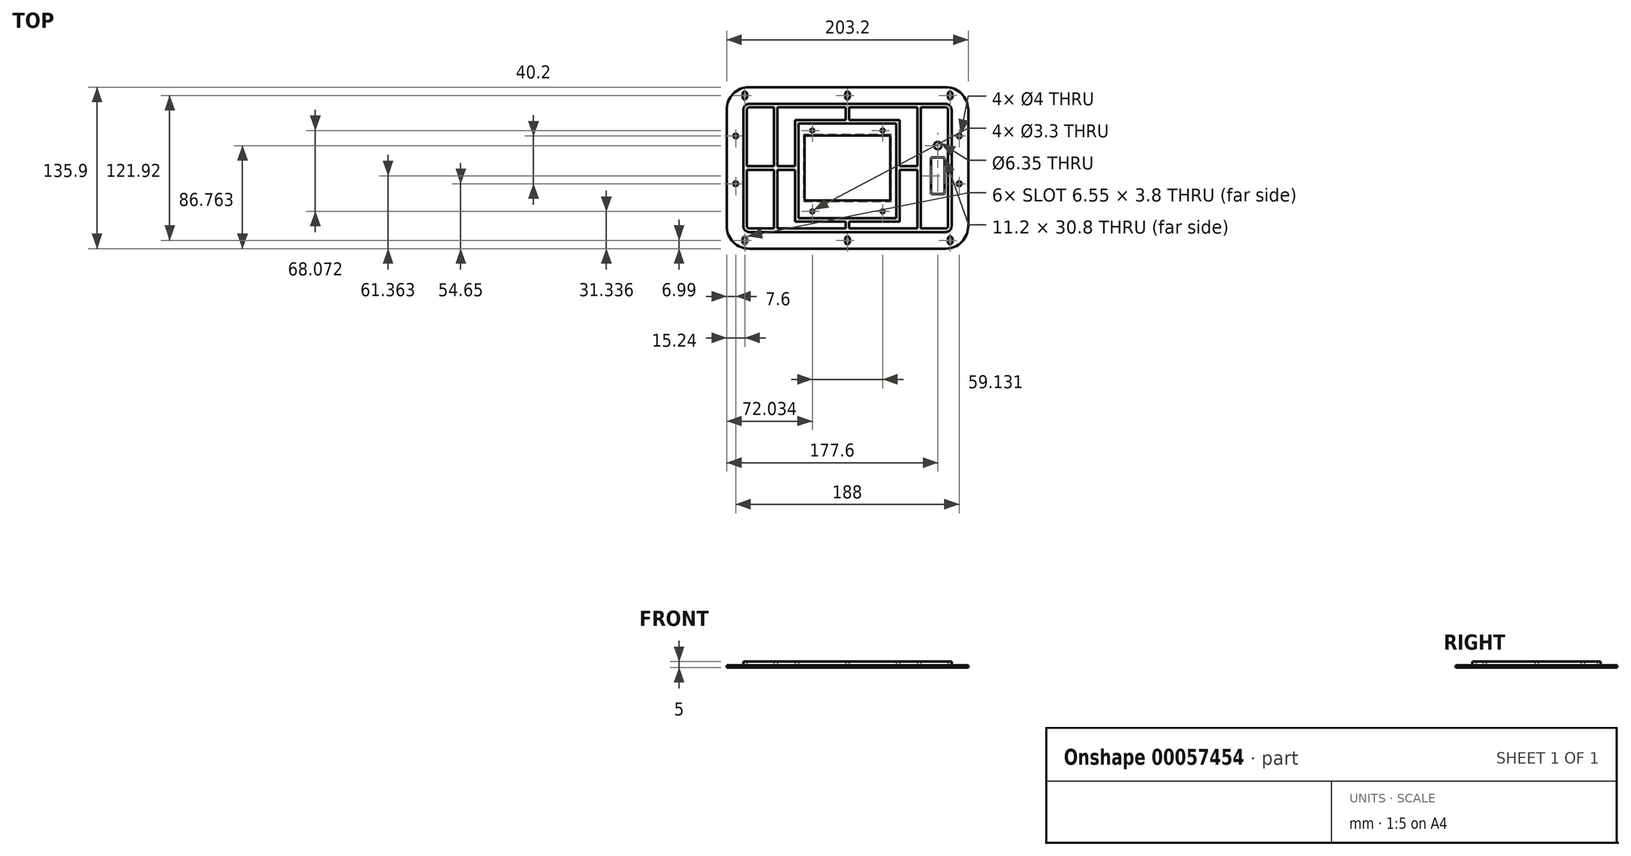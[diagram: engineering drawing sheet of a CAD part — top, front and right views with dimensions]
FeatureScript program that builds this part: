
annotation { "Feature Type Name" : "Feature", "Feature Type Description" : "" }
export const myFeature = defineFeature(function(context is Context, id is Id, definition is map)
    precondition{}
    {
        {
            var Q0;
            Q0=qCreatedBy(makeId("Top.planeOp"),FACE);
            var sketch = newSketch(context, id + "F0", { "sketchPlane" : qUnion([Q0])});
            skLineSegment(sketch, "E0.rect.bottom", {"start": v(82.55, -67.95) * mm, "end": v(-82.55, -67.95) * mm});
            skLineSegment(sketch, "E0.rect.top", {"start": v(82.55, 67.95) * mm, "end": v(-82.55, 67.95) * mm});
            skLineSegment(sketch, "E0.rect.left", {"start": v(101.6, -48.9) * mm, "end": v(101.6, 48.9) * mm});
            skLineSegment(sketch, "E0.rect.right", {"start": v(-101.6, -48.9) * mm, "end": v(-101.6, 48.9) * mm});
            skPoint(sketch, "E0.rect.middle", {"position": v(0, 0) * mm});
            skPoint(sketch, "E1.visualSharp", {"position": v(101.6, -67.94) * mm});
            skArc(sketch, "E1.filletArc", {"start": v(82.55, -67.95) * mm, "mid": v(96.02, -62.37) * mm, "end": v(101.6, -48.9) * mm});
            skPoint(sketch, "E2.visualSharp", {"position": v(101.6, 67.95) * mm});
            skArc(sketch, "E2.filletArc", {"start": v(101.6, 48.9) * mm, "mid": v(96.02, 62.37) * mm, "end": v(82.55, 67.95) * mm});
            skPoint(sketch, "E3.visualSharp", {"position": v(-101.6, 67.95) * mm});
            skArc(sketch, "E3.filletArc", {"start": v(-82.55, 67.95) * mm, "mid": v(-96.02, 62.37) * mm, "end": v(-101.6, 48.9) * mm});
            skPoint(sketch, "E4.visualSharp", {"position": v(-101.6, -67.95) * mm});
            skArc(sketch, "E4.filletArc", {"start": v(-101.6, -48.9) * mm, "mid": v(-96.02, -62.37) * mm, "end": v(-82.55, -67.95) * mm});
            skLineSegment(sketch, "E5", {"start": v(0, 60.96) * mm, "end": v(0, -60.96) * mm, "construction": true});
            skLineSegment(sketch, "E6", {"start": v(-86.36, -59.59) * mm, "end": v(-86.36, -62.33) * mm, "construction": true});
            skPoint(sketch, "E7", {"position": v(-86.36, -60.96) * mm});
            skLineSegment(sketch, "E8", {"start": v(-86.36, -60.96) * mm, "end": v(86.36, -60.96) * mm, "construction": true});
            skLineSegment(sketch, "E9", {"start": v(-88.26, -60.96) * mm, "end": v(-84.46, -60.96) * mm, "construction": true});
            skLineSegment(sketch, "E10", {"start": v(-84.46, -62.33) * mm, "end": v(-84.46, -59.59) * mm});
            skLineSegment(sketch, "E11", {"start": v(-88.26, -59.59) * mm, "end": v(-88.26, -62.34) * mm});
            skArc(sketch, "E12", {"start": v(-88.26, -59.59) * mm, "mid": v(-86.36, -57.68) * mm, "end": v(-84.46, -59.59) * mm});
            skArc(sketch, "E13", {"start": v(-84.46, -62.33) * mm, "mid": v(-86.36, -64.23) * mm, "end": v(-88.26, -62.34) * mm});
            skArc(sketch, "E14.0.1.0", {"start": v(-84.46, 59.59) * mm, "mid": v(-86.36, 57.68) * mm, "end": v(-88.26, 59.59) * mm});
            skArc(sketch, "E14.0.1.1", {"start": v(-88.26, 62.33) * mm, "mid": v(-86.36, 64.23) * mm, "end": v(-84.46, 62.33) * mm});
            skLineSegment(sketch, "E14.0.1.2", {"start": v(-84.46, 59.59) * mm, "end": v(-84.46, 62.34) * mm});
            skLineSegment(sketch, "E14.0.1.3", {"start": v(-88.26, 62.34) * mm, "end": v(-88.26, 59.59) * mm});
            skLineSegment(sketch, "E14.0.1.4", {"start": v(-88.26, 60.96) * mm, "end": v(-84.46, 60.96) * mm, "construction": true});
            skLineSegment(sketch, "E14.0.1.5", {"start": v(-86.36, 62.33) * mm, "end": v(-86.36, 59.58) * mm, "construction": true});
            skArc(sketch, "E14.1.0.0", {"start": v(1.9, -62.33) * mm, "mid": v(0, -64.23) * mm, "end": v(-1.9, -62.34) * mm});
            skArc(sketch, "E14.1.0.1", {"start": v(-1.9, -59.59) * mm, "mid": v(0, -57.68) * mm, "end": v(1.9, -59.59) * mm});
            skLineSegment(sketch, "E14.1.0.2", {"start": v(1.9, -62.33) * mm, "end": v(1.9, -59.59) * mm});
            skLineSegment(sketch, "E14.1.0.3", {"start": v(-1.9, -59.59) * mm, "end": v(-1.9, -62.34) * mm});
            skLineSegment(sketch, "E14.1.0.4", {"start": v(-1.9, -60.96) * mm, "end": v(1.9, -60.96) * mm, "construction": true});
            skLineSegment(sketch, "E14.1.0.5", {"start": v(0, -59.58) * mm, "end": v(0, -62.33) * mm, "construction": true});
            skArc(sketch, "E14.1.1.0", {"start": v(1.9, 59.59) * mm, "mid": v(0, 57.69) * mm, "end": v(-1.9, 59.59) * mm});
            skArc(sketch, "E14.1.1.1", {"start": v(-1.9, 62.33) * mm, "mid": v(0, 64.24) * mm, "end": v(1.9, 62.33) * mm});
            skLineSegment(sketch, "E14.1.1.2", {"start": v(1.9, 59.59) * mm, "end": v(1.9, 62.33) * mm});
            skLineSegment(sketch, "E14.1.1.3", {"start": v(-1.9, 62.33) * mm, "end": v(-1.9, 59.59) * mm});
            skLineSegment(sketch, "E14.1.1.4", {"start": v(-1.9, 60.96) * mm, "end": v(1.9, 60.96) * mm, "construction": true});
            skLineSegment(sketch, "E14.1.1.5", {"start": v(0, 62.34) * mm, "end": v(0, 59.59) * mm, "construction": true});
            skArc(sketch, "E14.2.0.0", {"start": v(88.26, -62.33) * mm, "mid": v(86.36, -64.23) * mm, "end": v(84.46, -62.34) * mm});
            skArc(sketch, "E14.2.0.1", {"start": v(84.46, -59.59) * mm, "mid": v(86.36, -57.68) * mm, "end": v(88.26, -59.59) * mm});
            skLineSegment(sketch, "E14.2.0.2", {"start": v(88.26, -62.33) * mm, "end": v(88.26, -59.59) * mm});
            skLineSegment(sketch, "E14.2.0.3", {"start": v(84.46, -59.59) * mm, "end": v(84.46, -62.34) * mm});
            skLineSegment(sketch, "E14.2.0.4", {"start": v(84.46, -60.96) * mm, "end": v(88.26, -60.96) * mm, "construction": true});
            skLineSegment(sketch, "E14.2.0.5", {"start": v(86.36, -59.58) * mm, "end": v(86.36, -62.33) * mm, "construction": true});
            skArc(sketch, "E14.2.1.0", {"start": v(88.26, 59.59) * mm, "mid": v(86.36, 57.69) * mm, "end": v(84.46, 59.59) * mm});
            skArc(sketch, "E14.2.1.1", {"start": v(84.46, 62.33) * mm, "mid": v(86.36, 64.24) * mm, "end": v(88.26, 62.33) * mm});
            skLineSegment(sketch, "E14.2.1.2", {"start": v(88.26, 59.59) * mm, "end": v(88.26, 62.33) * mm});
            skLineSegment(sketch, "E14.2.1.3", {"start": v(84.46, 62.33) * mm, "end": v(84.46, 59.59) * mm});
            skLineSegment(sketch, "E14.2.1.4", {"start": v(84.46, 60.96) * mm, "end": v(88.26, 60.96) * mm, "construction": true});
            skLineSegment(sketch, "E14.2.1.5", {"start": v(86.36, 62.34) * mm, "end": v(86.36, 59.59) * mm, "construction": true});
            skLineSegment(sketch, "E14.direction1", {"start": v(-88.26, -62.34) * mm, "end": v(-1.9, -62.34) * mm, "construction": true});
            skLineSegment(sketch, "E14.direction2", {"start": v(-88.26, -62.34) * mm, "end": v(-88.26, 59.59) * mm, "construction": true});
            skPoint(sketch, "E15", {"position": v(-94, -13.3) * mm});
            skCircle(sketch, "E16", {"center": v(-94, -13.3) * mm, "radius": 2 * mm});
            skCircle(sketch, "E17.0.1.0", {"center": v(-94, 26.9) * mm, "radius": 2 * mm});
            skCircle(sketch, "E17.1.0.0", {"center": v(94, -13.3) * mm, "radius": 2 * mm});
            skCircle(sketch, "E17.1.1.0", {"center": v(94, 26.9) * mm, "radius": 2 * mm});
            skLineSegment(sketch, "E17.direction1", {"start": v(-94, -13.3) * mm, "end": v(94, -13.3) * mm, "construction": true});
            skLineSegment(sketch, "E17.direction2", {"start": v(-94, -13.3) * mm, "end": v(-94, 26.9) * mm, "construction": true});
            skLineSegment(sketch, "E18.bottom", {"start": v(70.4, 8.81) * mm, "end": v(81.6, 8.81) * mm});
            skLineSegment(sketch, "E18.top", {"start": v(70.4, -21.99) * mm, "end": v(81.6, -21.99) * mm});
            skLineSegment(sketch, "E18.left", {"start": v(70.4, 8.81) * mm, "end": v(70.4, -21.99) * mm});
            skLineSegment(sketch, "E18.right", {"start": v(81.6, 8.81) * mm, "end": v(81.6, -21.99) * mm});
            skLineSegment(sketch, "E19", {"start": v(76, 8.81) * mm, "end": v(76, 18.81) * mm, "construction": true});
            skCircle(sketch, "E20", {"center": v(76, 18.81) * mm, "radius": 3.18 * mm});
            skLineSegment(sketch, "E21", {"start": v(76, 21.99) * mm, "end": v(76, 67.95) * mm, "construction": true});
            skLineSegment(sketch, "E22", {"start": v(76, -21.99) * mm, "end": v(76, -67.95) * mm, "construction": true});
            skSolve(sketch);
        }
        {
            var Q0;
            Q0=makeQuery(id+"F0.imprint","IMPRINT",FACE,{"disambiguationData":[TD([[makeQuery(id+"F0.imprint","IMPRINT",EDGE,{"derivedFrom":sQuery(id+"F0.wireOp",EDGE,"E0.rect.bottom")}),-1.0]])]});
            extrude(context, id + "F1", {"entities" : qUnion([Q0]), "depth" : 2 * mm});
        }
        {
            var Q0;
            Q0=makeQuery(id+"F1.opExtrude","CAP_FACE",FACE,{"disambiguationData":[OSD([sQuery(id+"F0.wireOp",EDGE,"E0.rect.bottom"),sQuery(id+"F0.wireOp",EDGE,"E0.rect.top"),sQuery(id+"F0.wireOp",EDGE,"E0.rect.left"),sQuery(id+"F0.wireOp",EDGE,"E0.rect.right"),sQuery(id+"F0.wireOp",EDGE,"E1.filletArc"),sQuery(id+"F0.wireOp",EDGE,"E2.filletArc"),sQuery(id+"F0.wireOp",EDGE,"E3.filletArc"),sQuery(id+"F0.wireOp",EDGE,"E4.filletArc"),sQuery(id+"F0.wireOp",EDGE,"E10"),sQuery(id+"F0.wireOp",EDGE,"E11"),sQuery(id+"F0.wireOp",EDGE,"E12"),sQuery(id+"F0.wireOp",EDGE,"E13"),sQuery(id+"F0.wireOp",EDGE,"E14.0.1.0"),sQuery(id+"F0.wireOp",EDGE,"E14.0.1.1"),sQuery(id+"F0.wireOp",EDGE,"E14.0.1.2"),sQuery(id+"F0.wireOp",EDGE,"E14.0.1.3"),sQuery(id+"F0.wireOp",EDGE,"E14.1.0.0"),sQuery(id+"F0.wireOp",EDGE,"E14.1.0.1"),sQuery(id+"F0.wireOp",EDGE,"E14.1.0.2"),sQuery(id+"F0.wireOp",EDGE,"E14.1.0.3"),sQuery(id+"F0.wireOp",EDGE,"E14.1.1.0"),sQuery(id+"F0.wireOp",EDGE,"E14.1.1.1"),sQuery(id+"F0.wireOp",EDGE,"E14.1.1.2"),sQuery(id+"F0.wireOp",EDGE,"E14.1.1.3"),sQuery(id+"F0.wireOp",EDGE,"E14.2.0.0"),sQuery(id+"F0.wireOp",EDGE,"E14.2.0.1"),sQuery(id+"F0.wireOp",EDGE,"E14.2.0.2"),sQuery(id+"F0.wireOp",EDGE,"E14.2.0.3"),sQuery(id+"F0.wireOp",EDGE,"E14.2.1.0"),sQuery(id+"F0.wireOp",EDGE,"E14.2.1.1"),sQuery(id+"F0.wireOp",EDGE,"E14.2.1.2"),sQuery(id+"F0.wireOp",EDGE,"E14.2.1.3"),sQuery(id+"F0.wireOp",EDGE,"E16"),sQuery(id+"F0.wireOp",EDGE,"E17.0.1.0"),sQuery(id+"F0.wireOp",EDGE,"E17.1.0.0"),sQuery(id+"F0.wireOp",EDGE,"E17.1.1.0")])],"isStart":false});
            var sketch = newSketch(context, id + "F2", { "sketchPlane" : qUnion([Q0])});
            skLineSegment(sketch, "E23.rect.bottom", {"start": v(36.04, -27.28) * mm, "end": v(-36.04, -27.28) * mm});
            skLineSegment(sketch, "E23.rect.top", {"start": v(36.04, 27.28) * mm, "end": v(-36.04, 27.28) * mm});
            skLineSegment(sketch, "E23.rect.left", {"start": v(36.04, -27.28) * mm, "end": v(36.04, 27.28) * mm});
            skLineSegment(sketch, "E23.rect.right", {"start": v(-36.04, -27.28) * mm, "end": v(-36.04, 27.28) * mm});
            skPoint(sketch, "E23.rect.middle", {"position": v(0, 0) * mm});
            skPoint(sketch, "E24", {"position": v(-29.57, -36.61) * mm});
            skCircle(sketch, "E25", {"center": v(-29.57, -36.61) * mm, "radius": 1.65 * mm});
            skPoint(sketch, "E26.0.1.0", {"position": v(-29.57, 31.46) * mm});
            skCircle(sketch, "E26.0.1.1", {"center": v(-29.57, 31.46) * mm, "radius": 1.65 * mm});
            skPoint(sketch, "E26.1.0.0", {"position": v(29.57, -36.61) * mm});
            skCircle(sketch, "E26.1.0.1", {"center": v(29.57, -36.61) * mm, "radius": 1.65 * mm});
            skPoint(sketch, "E26.1.1.0", {"position": v(29.57, 31.46) * mm});
            skCircle(sketch, "E26.1.1.1", {"center": v(29.57, 31.46) * mm, "radius": 1.65 * mm});
            skLineSegment(sketch, "E26.direction1", {"start": v(-29.57, -36.61) * mm, "end": v(29.57, -36.61) * mm, "construction": true});
            skLineSegment(sketch, "E26.direction2", {"start": v(-29.57, -36.61) * mm, "end": v(-29.57, 31.46) * mm, "construction": true});
            skSolve(sketch);
        }
        {
            var Q0;
            Q0=makeQuery(id+"F2.imprint","IMPRINT",FACE,{"disambiguationData":[TD([[makeQuery(id+"F2.imprint","IMPRINT",EDGE,{"derivedFrom":sQuery(id+"F2.wireOp",EDGE,"E23.rect.bottom")}),-1.0]])]});
            var Q1;
            Q1=makeQuery(id+"F2.imprint","IMPRINT",FACE,{"disambiguationData":[TD([[makeQuery(id+"F2.imprint","IMPRINT",EDGE,{"derivedFrom":sQuery(id+"F2.wireOp",EDGE,"E26.0.1.1")}),1.0]])]});
            var Q2;
            Q2=makeQuery(id+"F2.imprint","IMPRINT",FACE,{"disambiguationData":[TD([[makeQuery(id+"F2.imprint","IMPRINT",EDGE,{"derivedFrom":sQuery(id+"F2.wireOp",EDGE,"E26.1.1.1")}),1.0]])]});
            var Q3;
            Q3=makeQuery(id+"F2.imprint","IMPRINT",FACE,{"disambiguationData":[TD([[makeQuery(id+"F2.imprint","IMPRINT",EDGE,{"derivedFrom":sQuery(id+"F2.wireOp",EDGE,"E26.1.0.1")}),1.0]])]});
            var Q4;
            Q4=makeQuery(id+"F2.imprint","IMPRINT",FACE,{"disambiguationData":[TD([[makeQuery(id+"F2.imprint","IMPRINT",EDGE,{"derivedFrom":sQuery(id+"F2.wireOp",EDGE,"E25")}),1.0]])]});
            extrude(context, id + "F3", {"entities" : qUnion([Q0, Q1, Q2, Q3, Q4]), "operationType" : NewBodyOperationType.REMOVE, "endBound" : BoundingType.THROUGH_ALL, "oppositeDirection" : true, "depth" : 25 * mm});
        }
        {
            var Q0;
            Q0=makeQuery(id+"F3.boolean.opBoolean","INTERSECT",EDGE,{"derivedFrom":[makeQuery(id+"F1.opExtrude","CAP_FACE",FACE,{"disambiguationData":[OSD([sQuery(id+"F0.wireOp",EDGE,"E0.rect.bottom"),sQuery(id+"F0.wireOp",EDGE,"E0.rect.top"),sQuery(id+"F0.wireOp",EDGE,"E0.rect.left"),sQuery(id+"F0.wireOp",EDGE,"E0.rect.right"),sQuery(id+"F0.wireOp",EDGE,"E1.filletArc"),sQuery(id+"F0.wireOp",EDGE,"E2.filletArc"),sQuery(id+"F0.wireOp",EDGE,"E3.filletArc"),sQuery(id+"F0.wireOp",EDGE,"E4.filletArc"),sQuery(id+"F0.wireOp",EDGE,"E10"),sQuery(id+"F0.wireOp",EDGE,"E11"),sQuery(id+"F0.wireOp",EDGE,"E12"),sQuery(id+"F0.wireOp",EDGE,"E13"),sQuery(id+"F0.wireOp",EDGE,"E14.0.1.0"),sQuery(id+"F0.wireOp",EDGE,"E14.0.1.1"),sQuery(id+"F0.wireOp",EDGE,"E14.0.1.2"),sQuery(id+"F0.wireOp",EDGE,"E14.0.1.3"),sQuery(id+"F0.wireOp",EDGE,"E14.1.0.0"),sQuery(id+"F0.wireOp",EDGE,"E14.1.0.1"),sQuery(id+"F0.wireOp",EDGE,"E14.1.0.2"),sQuery(id+"F0.wireOp",EDGE,"E14.1.0.3"),sQuery(id+"F0.wireOp",EDGE,"E14.1.1.0"),sQuery(id+"F0.wireOp",EDGE,"E14.1.1.1"),sQuery(id+"F0.wireOp",EDGE,"E14.1.1.2"),sQuery(id+"F0.wireOp",EDGE,"E14.1.1.3"),sQuery(id+"F0.wireOp",EDGE,"E14.2.0.0"),sQuery(id+"F0.wireOp",EDGE,"E14.2.0.1"),sQuery(id+"F0.wireOp",EDGE,"E14.2.0.2"),sQuery(id+"F0.wireOp",EDGE,"E14.2.0.3"),sQuery(id+"F0.wireOp",EDGE,"E14.2.1.0"),sQuery(id+"F0.wireOp",EDGE,"E14.2.1.1"),sQuery(id+"F0.wireOp",EDGE,"E14.2.1.2"),sQuery(id+"F0.wireOp",EDGE,"E14.2.1.3"),sQuery(id+"F0.wireOp",EDGE,"E16"),sQuery(id+"F0.wireOp",EDGE,"E17.0.1.0"),sQuery(id+"F0.wireOp",EDGE,"E17.1.0.0"),sQuery(id+"F0.wireOp",EDGE,"E17.1.1.0"),sQuery(id+"F0.wireOp",EDGE,"E18.bottom"),sQuery(id+"F0.wireOp",EDGE,"E18.top"),sQuery(id+"F0.wireOp",EDGE,"E18.left"),sQuery(id+"F0.wireOp",EDGE,"E18.right"),sQuery(id+"F0.wireOp",EDGE,"E20")])],"isStart":true}),makeQuery(id+"F3.opExtrude","SWEPT_FACE",FACE,{"disambiguationData":[OSD([sQuery(id+"F2.wireOp",EDGE,"E23.rect.top")])]})]});
            var Q1;
            Q1=makeQuery(id+"F3.boolean.opBoolean","INTERSECT",EDGE,{"derivedFrom":[makeQuery(id+"F1.opExtrude","CAP_FACE",FACE,{"disambiguationData":[OSD([sQuery(id+"F0.wireOp",EDGE,"E0.rect.bottom"),sQuery(id+"F0.wireOp",EDGE,"E0.rect.top"),sQuery(id+"F0.wireOp",EDGE,"E0.rect.left"),sQuery(id+"F0.wireOp",EDGE,"E0.rect.right"),sQuery(id+"F0.wireOp",EDGE,"E1.filletArc"),sQuery(id+"F0.wireOp",EDGE,"E2.filletArc"),sQuery(id+"F0.wireOp",EDGE,"E3.filletArc"),sQuery(id+"F0.wireOp",EDGE,"E4.filletArc"),sQuery(id+"F0.wireOp",EDGE,"E10"),sQuery(id+"F0.wireOp",EDGE,"E11"),sQuery(id+"F0.wireOp",EDGE,"E12"),sQuery(id+"F0.wireOp",EDGE,"E13"),sQuery(id+"F0.wireOp",EDGE,"E14.0.1.0"),sQuery(id+"F0.wireOp",EDGE,"E14.0.1.1"),sQuery(id+"F0.wireOp",EDGE,"E14.0.1.2"),sQuery(id+"F0.wireOp",EDGE,"E14.0.1.3"),sQuery(id+"F0.wireOp",EDGE,"E14.1.0.0"),sQuery(id+"F0.wireOp",EDGE,"E14.1.0.1"),sQuery(id+"F0.wireOp",EDGE,"E14.1.0.2"),sQuery(id+"F0.wireOp",EDGE,"E14.1.0.3"),sQuery(id+"F0.wireOp",EDGE,"E14.1.1.0"),sQuery(id+"F0.wireOp",EDGE,"E14.1.1.1"),sQuery(id+"F0.wireOp",EDGE,"E14.1.1.2"),sQuery(id+"F0.wireOp",EDGE,"E14.1.1.3"),sQuery(id+"F0.wireOp",EDGE,"E14.2.0.0"),sQuery(id+"F0.wireOp",EDGE,"E14.2.0.1"),sQuery(id+"F0.wireOp",EDGE,"E14.2.0.2"),sQuery(id+"F0.wireOp",EDGE,"E14.2.0.3"),sQuery(id+"F0.wireOp",EDGE,"E14.2.1.0"),sQuery(id+"F0.wireOp",EDGE,"E14.2.1.1"),sQuery(id+"F0.wireOp",EDGE,"E14.2.1.2"),sQuery(id+"F0.wireOp",EDGE,"E14.2.1.3"),sQuery(id+"F0.wireOp",EDGE,"E16"),sQuery(id+"F0.wireOp",EDGE,"E17.0.1.0"),sQuery(id+"F0.wireOp",EDGE,"E17.1.0.0"),sQuery(id+"F0.wireOp",EDGE,"E17.1.1.0"),sQuery(id+"F0.wireOp",EDGE,"E18.bottom"),sQuery(id+"F0.wireOp",EDGE,"E18.top"),sQuery(id+"F0.wireOp",EDGE,"E18.left"),sQuery(id+"F0.wireOp",EDGE,"E18.right"),sQuery(id+"F0.wireOp",EDGE,"E20")])],"isStart":true}),makeQuery(id+"F3.opExtrude","SWEPT_FACE",FACE,{"disambiguationData":[OSD([sQuery(id+"F2.wireOp",EDGE,"E23.rect.left")])]})]});
            var Q2;
            Q2=makeQuery(id+"F3.boolean.opBoolean","INTERSECT",EDGE,{"derivedFrom":[makeQuery(id+"F1.opExtrude","CAP_FACE",FACE,{"disambiguationData":[OSD([sQuery(id+"F0.wireOp",EDGE,"E0.rect.bottom"),sQuery(id+"F0.wireOp",EDGE,"E0.rect.top"),sQuery(id+"F0.wireOp",EDGE,"E0.rect.left"),sQuery(id+"F0.wireOp",EDGE,"E0.rect.right"),sQuery(id+"F0.wireOp",EDGE,"E1.filletArc"),sQuery(id+"F0.wireOp",EDGE,"E2.filletArc"),sQuery(id+"F0.wireOp",EDGE,"E3.filletArc"),sQuery(id+"F0.wireOp",EDGE,"E4.filletArc"),sQuery(id+"F0.wireOp",EDGE,"E10"),sQuery(id+"F0.wireOp",EDGE,"E11"),sQuery(id+"F0.wireOp",EDGE,"E12"),sQuery(id+"F0.wireOp",EDGE,"E13"),sQuery(id+"F0.wireOp",EDGE,"E14.0.1.0"),sQuery(id+"F0.wireOp",EDGE,"E14.0.1.1"),sQuery(id+"F0.wireOp",EDGE,"E14.0.1.2"),sQuery(id+"F0.wireOp",EDGE,"E14.0.1.3"),sQuery(id+"F0.wireOp",EDGE,"E14.1.0.0"),sQuery(id+"F0.wireOp",EDGE,"E14.1.0.1"),sQuery(id+"F0.wireOp",EDGE,"E14.1.0.2"),sQuery(id+"F0.wireOp",EDGE,"E14.1.0.3"),sQuery(id+"F0.wireOp",EDGE,"E14.1.1.0"),sQuery(id+"F0.wireOp",EDGE,"E14.1.1.1"),sQuery(id+"F0.wireOp",EDGE,"E14.1.1.2"),sQuery(id+"F0.wireOp",EDGE,"E14.1.1.3"),sQuery(id+"F0.wireOp",EDGE,"E14.2.0.0"),sQuery(id+"F0.wireOp",EDGE,"E14.2.0.1"),sQuery(id+"F0.wireOp",EDGE,"E14.2.0.2"),sQuery(id+"F0.wireOp",EDGE,"E14.2.0.3"),sQuery(id+"F0.wireOp",EDGE,"E14.2.1.0"),sQuery(id+"F0.wireOp",EDGE,"E14.2.1.1"),sQuery(id+"F0.wireOp",EDGE,"E14.2.1.2"),sQuery(id+"F0.wireOp",EDGE,"E14.2.1.3"),sQuery(id+"F0.wireOp",EDGE,"E16"),sQuery(id+"F0.wireOp",EDGE,"E17.0.1.0"),sQuery(id+"F0.wireOp",EDGE,"E17.1.0.0"),sQuery(id+"F0.wireOp",EDGE,"E17.1.1.0"),sQuery(id+"F0.wireOp",EDGE,"E18.bottom"),sQuery(id+"F0.wireOp",EDGE,"E18.top"),sQuery(id+"F0.wireOp",EDGE,"E18.left"),sQuery(id+"F0.wireOp",EDGE,"E18.right"),sQuery(id+"F0.wireOp",EDGE,"E20")])],"isStart":true}),makeQuery(id+"F3.opExtrude","SWEPT_FACE",FACE,{"disambiguationData":[OSD([sQuery(id+"F2.wireOp",EDGE,"E23.rect.right")])]})]});
            var Q3;
            Q3=makeQuery(id+"F3.boolean.opBoolean","INTERSECT",EDGE,{"derivedFrom":[makeQuery(id+"F1.opExtrude","CAP_FACE",FACE,{"disambiguationData":[OSD([sQuery(id+"F0.wireOp",EDGE,"E0.rect.bottom"),sQuery(id+"F0.wireOp",EDGE,"E0.rect.top"),sQuery(id+"F0.wireOp",EDGE,"E0.rect.left"),sQuery(id+"F0.wireOp",EDGE,"E0.rect.right"),sQuery(id+"F0.wireOp",EDGE,"E1.filletArc"),sQuery(id+"F0.wireOp",EDGE,"E2.filletArc"),sQuery(id+"F0.wireOp",EDGE,"E3.filletArc"),sQuery(id+"F0.wireOp",EDGE,"E4.filletArc"),sQuery(id+"F0.wireOp",EDGE,"E10"),sQuery(id+"F0.wireOp",EDGE,"E11"),sQuery(id+"F0.wireOp",EDGE,"E12"),sQuery(id+"F0.wireOp",EDGE,"E13"),sQuery(id+"F0.wireOp",EDGE,"E14.0.1.0"),sQuery(id+"F0.wireOp",EDGE,"E14.0.1.1"),sQuery(id+"F0.wireOp",EDGE,"E14.0.1.2"),sQuery(id+"F0.wireOp",EDGE,"E14.0.1.3"),sQuery(id+"F0.wireOp",EDGE,"E14.1.0.0"),sQuery(id+"F0.wireOp",EDGE,"E14.1.0.1"),sQuery(id+"F0.wireOp",EDGE,"E14.1.0.2"),sQuery(id+"F0.wireOp",EDGE,"E14.1.0.3"),sQuery(id+"F0.wireOp",EDGE,"E14.1.1.0"),sQuery(id+"F0.wireOp",EDGE,"E14.1.1.1"),sQuery(id+"F0.wireOp",EDGE,"E14.1.1.2"),sQuery(id+"F0.wireOp",EDGE,"E14.1.1.3"),sQuery(id+"F0.wireOp",EDGE,"E14.2.0.0"),sQuery(id+"F0.wireOp",EDGE,"E14.2.0.1"),sQuery(id+"F0.wireOp",EDGE,"E14.2.0.2"),sQuery(id+"F0.wireOp",EDGE,"E14.2.0.3"),sQuery(id+"F0.wireOp",EDGE,"E14.2.1.0"),sQuery(id+"F0.wireOp",EDGE,"E14.2.1.1"),sQuery(id+"F0.wireOp",EDGE,"E14.2.1.2"),sQuery(id+"F0.wireOp",EDGE,"E14.2.1.3"),sQuery(id+"F0.wireOp",EDGE,"E16"),sQuery(id+"F0.wireOp",EDGE,"E17.0.1.0"),sQuery(id+"F0.wireOp",EDGE,"E17.1.0.0"),sQuery(id+"F0.wireOp",EDGE,"E17.1.1.0"),sQuery(id+"F0.wireOp",EDGE,"E18.bottom"),sQuery(id+"F0.wireOp",EDGE,"E18.top"),sQuery(id+"F0.wireOp",EDGE,"E18.left"),sQuery(id+"F0.wireOp",EDGE,"E18.right"),sQuery(id+"F0.wireOp",EDGE,"E20")])],"isStart":true}),makeQuery(id+"F3.opExtrude","SWEPT_FACE",FACE,{"disambiguationData":[OSD([sQuery(id+"F2.wireOp",EDGE,"E23.rect.bottom")])]})]});
            chamfer(context, id + "F4", {"entities" : qUnion([Q0, Q1, Q2, Q3]), "width" : 1 * mm, "tangentPropagation" : true});
        }
        {
            var Q0;
            Q0=makeQuery(id+"F1.opExtrude","CAP_FACE",FACE,{"disambiguationData":[OSD([sQuery(id+"F0.wireOp",EDGE,"E0.rect.bottom"),sQuery(id+"F0.wireOp",EDGE,"E0.rect.top"),sQuery(id+"F0.wireOp",EDGE,"E0.rect.left"),sQuery(id+"F0.wireOp",EDGE,"E0.rect.right"),sQuery(id+"F0.wireOp",EDGE,"E1.filletArc"),sQuery(id+"F0.wireOp",EDGE,"E2.filletArc"),sQuery(id+"F0.wireOp",EDGE,"E3.filletArc"),sQuery(id+"F0.wireOp",EDGE,"E4.filletArc"),sQuery(id+"F0.wireOp",EDGE,"E10"),sQuery(id+"F0.wireOp",EDGE,"E11"),sQuery(id+"F0.wireOp",EDGE,"E12"),sQuery(id+"F0.wireOp",EDGE,"E13"),sQuery(id+"F0.wireOp",EDGE,"E14.0.1.0"),sQuery(id+"F0.wireOp",EDGE,"E14.0.1.1"),sQuery(id+"F0.wireOp",EDGE,"E14.0.1.2"),sQuery(id+"F0.wireOp",EDGE,"E14.0.1.3"),sQuery(id+"F0.wireOp",EDGE,"E14.1.0.0"),sQuery(id+"F0.wireOp",EDGE,"E14.1.0.1"),sQuery(id+"F0.wireOp",EDGE,"E14.1.0.2"),sQuery(id+"F0.wireOp",EDGE,"E14.1.0.3"),sQuery(id+"F0.wireOp",EDGE,"E14.1.1.0"),sQuery(id+"F0.wireOp",EDGE,"E14.1.1.1"),sQuery(id+"F0.wireOp",EDGE,"E14.1.1.2"),sQuery(id+"F0.wireOp",EDGE,"E14.1.1.3"),sQuery(id+"F0.wireOp",EDGE,"E14.2.0.0"),sQuery(id+"F0.wireOp",EDGE,"E14.2.0.1"),sQuery(id+"F0.wireOp",EDGE,"E14.2.0.2"),sQuery(id+"F0.wireOp",EDGE,"E14.2.0.3"),sQuery(id+"F0.wireOp",EDGE,"E14.2.1.0"),sQuery(id+"F0.wireOp",EDGE,"E14.2.1.1"),sQuery(id+"F0.wireOp",EDGE,"E14.2.1.2"),sQuery(id+"F0.wireOp",EDGE,"E14.2.1.3"),sQuery(id+"F0.wireOp",EDGE,"E16"),sQuery(id+"F0.wireOp",EDGE,"E17.0.1.0"),sQuery(id+"F0.wireOp",EDGE,"E17.1.0.0"),sQuery(id+"F0.wireOp",EDGE,"E17.1.1.0"),sQuery(id+"F0.wireOp",EDGE,"E18.bottom"),sQuery(id+"F0.wireOp",EDGE,"E18.top"),sQuery(id+"F0.wireOp",EDGE,"E18.left"),sQuery(id+"F0.wireOp",EDGE,"E18.right"),sQuery(id+"F0.wireOp",EDGE,"E20")])],"isStart":false});
            var sketch = newSketch(context, id + "F5", { "sketchPlane" : qUnion([Q0])});
            skArc(sketch, "E27.0", {"start": v(87.6, 48.9) * mm, "mid": v(86.12, 52.47) * mm, "end": v(82.55, 53.95) * mm});
            skLineSegment(sketch, "E27.1", {"start": v(87.6, -48.9) * mm, "end": v(87.6, 48.9) * mm});
            skLineSegment(sketch, "E27.2", {"start": v(82.55, 53.95) * mm, "end": v(-82.55, 53.95) * mm});
            skArc(sketch, "E27.3", {"start": v(82.55, -53.95) * mm, "mid": v(86.12, -52.47) * mm, "end": v(87.6, -48.9) * mm});
            skArc(sketch, "E27.4", {"start": v(-82.55, 53.95) * mm, "mid": v(-86.12, 52.47) * mm, "end": v(-87.6, 48.9) * mm});
            skLineSegment(sketch, "E27.5", {"start": v(-87.6, -48.9) * mm, "end": v(-87.6, 48.9) * mm});
            skArc(sketch, "E27.6", {"start": v(-87.6, -48.9) * mm, "mid": v(-86.12, -52.47) * mm, "end": v(-82.55, -53.95) * mm});
            skLineSegment(sketch, "E27.7", {"start": v(82.55, -53.95) * mm, "end": v(-82.55, -53.95) * mm});
            skArc(sketch, "E28.0", {"start": v(84.6, 48.9) * mm, "mid": v(84, 50.34) * mm, "end": v(82.55, 50.95) * mm});
            skLineSegment(sketch, "E28.1", {"start": v(84.6, -48.9) * mm, "end": v(84.6, 48.9) * mm});
            skLineSegment(sketch, "E28.2", {"start": v(82.55, 50.95) * mm, "end": v(61.82, 50.95) * mm});
            skArc(sketch, "E28.3", {"start": v(82.55, -50.95) * mm, "mid": v(84, -50.34) * mm, "end": v(84.6, -48.9) * mm});
            skArc(sketch, "E28.4", {"start": v(-82.55, 50.95) * mm, "mid": v(-84, 50.34) * mm, "end": v(-84.6, 48.9) * mm});
            skLineSegment(sketch, "E28.5", {"start": v(-84.6, -48.9) * mm, "end": v(-84.6, -1.5) * mm});
            skArc(sketch, "E28.6", {"start": v(-84.6, -48.9) * mm, "mid": v(-84, -50.34) * mm, "end": v(-82.55, -50.95) * mm});
            skLineSegment(sketch, "E28.7", {"start": v(82.55, -50.95) * mm, "end": v(61.82, -50.95) * mm});
            skLineSegment(sketch, "E29", {"start": v(-61.82, 50.95) * mm, "end": v(-61.82, 1.5) * mm});
            skLineSegment(sketch, "E30", {"start": v(-58.82, 50.95) * mm, "end": v(-58.82, 1.5) * mm});
            skLineSegment(sketch, "E31", {"start": v(-36.04, 0) * mm, "end": v(-58.82, 0) * mm, "construction": true});
            skLineSegment(sketch, "E32", {"start": v(-61.82, 0) * mm, "end": v(-84.6, 0) * mm, "construction": true});
            skLineSegment(sketch, "E33", {"start": v(58.82, 50.95) * mm, "end": v(58.82, 1.5) * mm});
            skLineSegment(sketch, "E34", {"start": v(61.82, 50.95) * mm, "end": v(61.82, -50.95) * mm});
            skLineSegment(sketch, "E35", {"start": v(84.6, 0) * mm, "end": v(61.82, 0) * mm, "construction": true});
            skLineSegment(sketch, "E36", {"start": v(58.82, 0) * mm, "end": v(36.04, 0) * mm, "construction": true});
            skLineSegment(sketch, "E37.trimOffspring", {"start": v(-61.82, 50.95) * mm, "end": v(-82.55, 50.95) * mm});
            skLineSegment(sketch, "E38.trimOffspring", {"start": v(-61.82, -50.95) * mm, "end": v(-82.55, -50.95) * mm});
            skLineSegment(sketch, "E39.trimOffspring", {"start": v(58.82, -50.95) * mm, "end": v(1.5, -50.95) * mm});
            skLineSegment(sketch, "E40.trimOffspring", {"start": v(58.82, 50.95) * mm, "end": v(1.5, 50.95) * mm});
            skLineSegment(sketch, "E41.0", {"start": v(41.04, 37.28) * mm, "end": v(-41.04, 37.28) * mm});
            skLineSegment(sketch, "E41.1", {"start": v(41.04, -42.28) * mm, "end": v(41.04, 37.28) * mm});
            skLineSegment(sketch, "E41.2", {"start": v(41.04, -42.28) * mm, "end": v(-41.04, -42.28) * mm});
            skLineSegment(sketch, "E41.3", {"start": v(-41.04, -42.28) * mm, "end": v(-41.04, 37.28) * mm});
            skLineSegment(sketch, "E42.0", {"start": v(44.04, 40.28) * mm, "end": v(1.5, 40.28) * mm});
            skLineSegment(sketch, "E42.1", {"start": v(44.04, -45.28) * mm, "end": v(44.04, -1.5) * mm});
            skLineSegment(sketch, "E42.2", {"start": v(44.04, -45.28) * mm, "end": v(1.5, -45.28) * mm});
            skLineSegment(sketch, "E42.3", {"start": v(-44.04, -45.28) * mm, "end": v(-44.04, -1.5) * mm});
            skLineSegment(sketch, "E43", {"start": v(44.04, 1.5) * mm, "end": v(58.82, 1.5) * mm});
            skLineSegment(sketch, "E44", {"start": v(44.04, -1.5) * mm, "end": v(58.82, -1.5) * mm});
            skLineSegment(sketch, "E45.trimOffspring", {"start": v(44.04, 1.5) * mm, "end": v(44.04, 40.28) * mm});
            skLineSegment(sketch, "E46.trimOffspring", {"start": v(58.82, -1.5) * mm, "end": v(58.82, -50.95) * mm});
            skLineSegment(sketch, "E47", {"start": v(-58.82, 1.5) * mm, "end": v(-44.04, 1.5) * mm});
            skLineSegment(sketch, "E48", {"start": v(-44.04, -1.5) * mm, "end": v(-58.82, -1.5) * mm});
            skLineSegment(sketch, "E49.trimOffspring", {"start": v(-58.82, -1.5) * mm, "end": v(-58.82, -50.95) * mm});
            skLineSegment(sketch, "E50.trimOffspring", {"start": v(-44.04, 1.5) * mm, "end": v(-44.04, 40.28) * mm});
            skLineSegment(sketch, "E51", {"start": v(-1.5, 50.95) * mm, "end": v(-1.5, 40.28) * mm});
            skLineSegment(sketch, "E52", {"start": v(1.5, 50.95) * mm, "end": v(1.5, 40.28) * mm});
            skLineSegment(sketch, "E53.trimOffspring", {"start": v(-1.5, 50.95) * mm, "end": v(-58.82, 50.95) * mm});
            skLineSegment(sketch, "E54.trimOffspring", {"start": v(-1.5, 40.28) * mm, "end": v(-44.04, 40.28) * mm});
            skLineSegment(sketch, "E55", {"start": v(1.5, -45.28) * mm, "end": v(1.5, -50.95) * mm});
            skLineSegment(sketch, "E56", {"start": v(-1.5, -45.28) * mm, "end": v(-1.5, -50.95) * mm});
            skLineSegment(sketch, "E57.trimOffspring", {"start": v(-1.5, -45.28) * mm, "end": v(-44.04, -45.28) * mm});
            skLineSegment(sketch, "E58.trimOffspring", {"start": v(-1.5, -50.95) * mm, "end": v(-58.82, -50.95) * mm});
            skLineSegment(sketch, "E59", {"start": v(-84.6, 1.5) * mm, "end": v(-61.82, 1.5) * mm});
            skLineSegment(sketch, "E60", {"start": v(-84.6, -1.5) * mm, "end": v(-61.82, -1.5) * mm});
            skLineSegment(sketch, "E61.trimOffspring", {"start": v(-84.6, 1.5) * mm, "end": v(-84.6, 48.9) * mm});
            skLineSegment(sketch, "E62.trimOffspring", {"start": v(-61.82, -1.5) * mm, "end": v(-61.82, -50.95) * mm});
            skSolve(sketch);
        }
        {
            var Q0;
            Q0=makeQuery(id+"F5.imprint","IMPRINT",FACE,{"disambiguationData":[TD([[makeQuery(id+"F5.imprint","IMPRINT",EDGE,{"derivedFrom":sQuery(id+"F5.wireOp",EDGE,"E27.0")}),1.0]])]});
            extrude(context, id + "F6", {"entities" : qUnion([Q0]), "operationType" : NewBodyOperationType.ADD, "depth" : 3 * mm});
        }
    });
